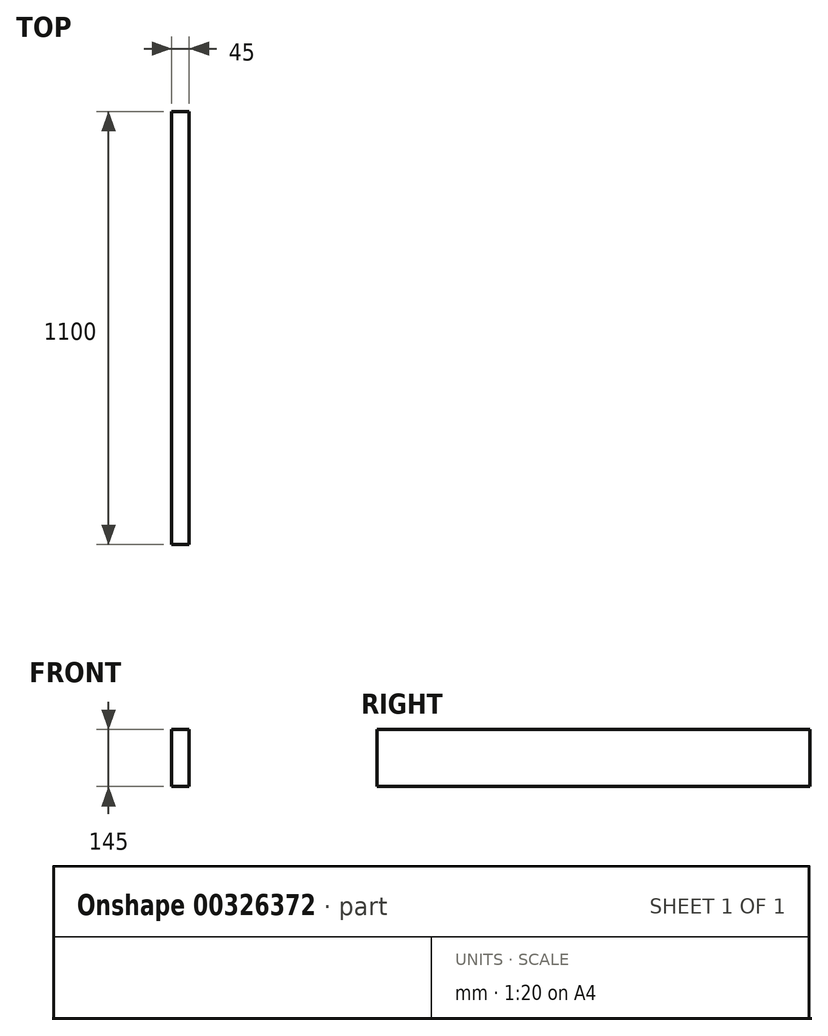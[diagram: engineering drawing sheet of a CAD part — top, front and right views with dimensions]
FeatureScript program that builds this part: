
annotation { "Feature Type Name" : "Feature", "Feature Type Description" : "" }
export const myFeature = defineFeature(function(context is Context, id is Id, definition is map)
    precondition{}
    {
        {
            var Q0;
            Q0=qCreatedBy(makeId("Front.planeOp"),FACE);
            var sketch = newSketch(context, id + "F0", { "sketchPlane" : qUnion([Q0])});
            skLineSegment(sketch, "E0.bottom", {"start": v(0, 0) * mm, "end": v(45, 0) * mm});
            skLineSegment(sketch, "E0.top", {"start": v(0, 145) * mm, "end": v(45, 145) * mm});
            skLineSegment(sketch, "E0.left", {"start": v(0, 0) * mm, "end": v(0, 145) * mm});
            skLineSegment(sketch, "E0.right", {"start": v(45, 0) * mm, "end": v(45, 145) * mm});
            skSolve(sketch);
        }
        {
            var Q0;
            Q0=makeQuery(id+"F0.imprint","IMPRINT",FACE,{"disambiguationData":[TD([[makeQuery(id+"F0.imprint","IMPRINT",EDGE,{"derivedFrom":sQuery(id+"F0.wireOp",EDGE,"E0.bottom")}),1.0]])]});
            extrude(context, id + "F1", {"entities" : qUnion([Q0]), "depth" : 1100 * mm});
        }
    });
